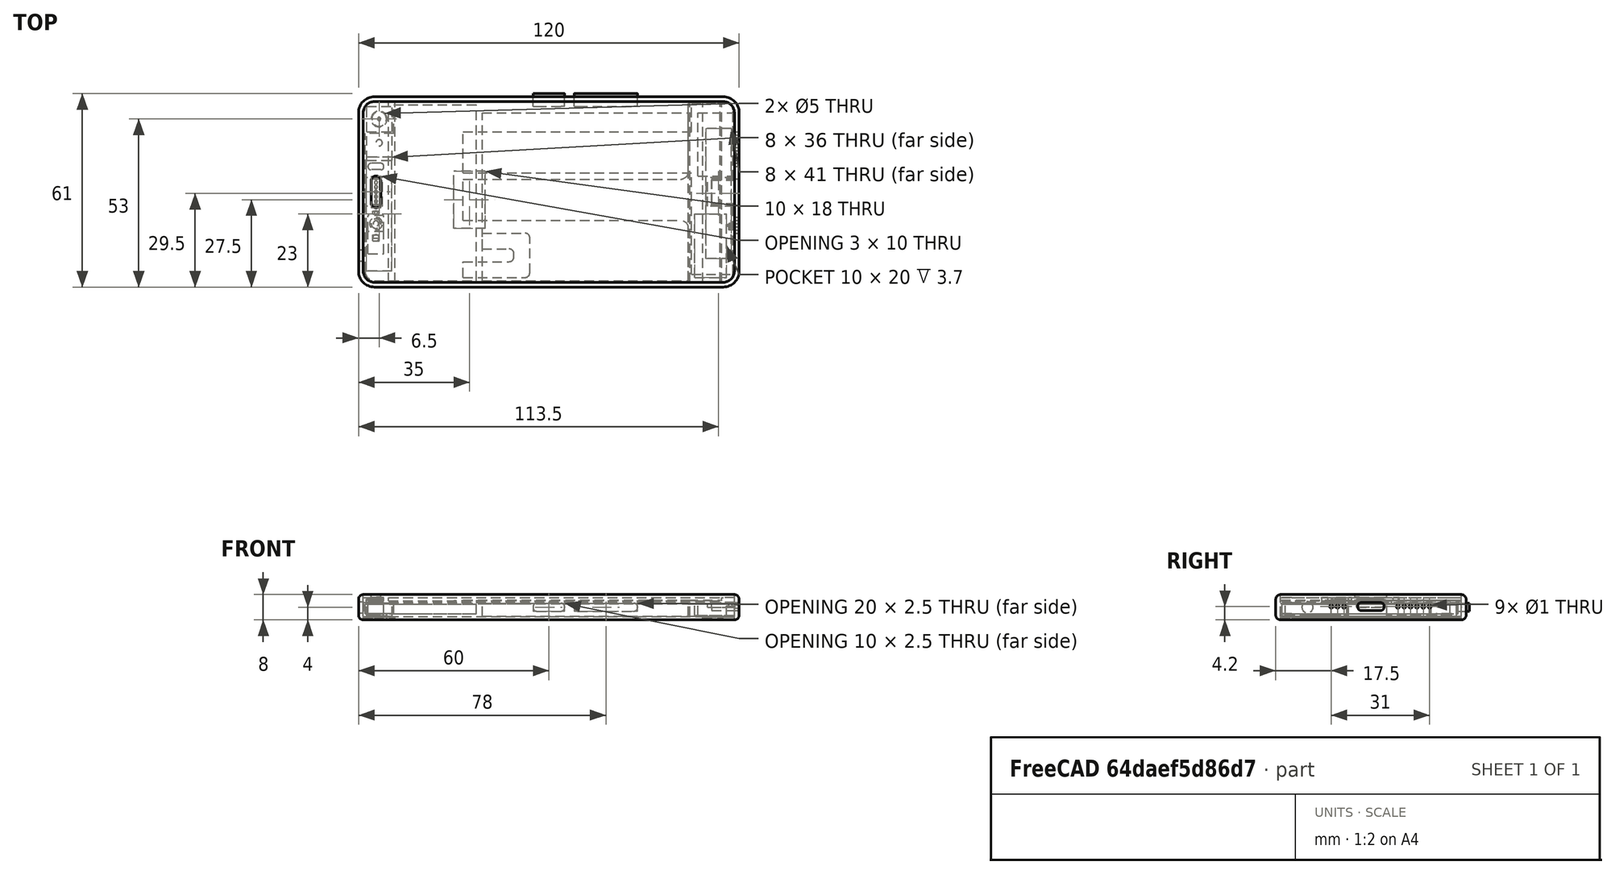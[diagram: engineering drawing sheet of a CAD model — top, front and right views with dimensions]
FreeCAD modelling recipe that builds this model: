
FCSTD DOCUMENT  (FreeCAD 0.16R6706 (Git))
Label: device
License: All rights reserved
LicenseURL: http://en.wikipedia.org/wiki/All_rights_reserved
objects: Part::Box×52, Part::Cut×34, Part::Cylinder×32, Part::Fillet×25, Part::MultiFuse×20, Part::Sphere×4, Part::Chamfer×1
note: 168 computed .brp shape members not serialized (recipe doc carries the construction recipe); baked Part::Feature solids carry a one-line shape summary decoded from their .brp

FEATURE [Part::Box] Box  label="Cubo"
  Height = 8
  Length = 120
  Width = 60
FEATURE [Part::Box] Box001  label="Cubo001"
  Height = 8
  Length = 117
  Placement = pos=(1.5,1.5,0) rot=(0,0,1;0rad)
  Width = 57
FEATURE [Part::Fillet] Fillet
  Base = -> Box
  Edges = 4 edges r=5: [Edge1,Edge3,Edge5,Edge7]
FEATURE [Part::Fillet] Fillet001
  Base = -> Fillet
  Edges = 16 edges r=1.5: [Edge1,Edge4,Edge5,Edge6,Edge7,Edge8,Edge9,Edge10,Edge11,Edge12,Edge14,Edge16,Edge17,Edge18,Edge19,Edge20]
FEATURE [Part::Fillet] Fillet002
  Base = -> Box001
  Edges = 4 edges r=3.5: [Edge1,Edge3,Edge5,Edge7]
  Placement = pos=(0,0,1) rot=(0,0,1;0rad)
FEATURE [Part::Box] Box002  label="Cubo002"
  Height = 1
  Length = 117
  Placement = pos=(1.5,1.5,0) rot=(0,0,1;0rad)
  Width = 57
FEATURE [Part::Fillet] Fillet003
  Base = -> Box002
  Edges = 4 edges r=3.5: [Edge1,Edge3,Edge5,Edge7]
  Placement = pos=(0,0,7) rot=(0,0,1;0rad)
FEATURE [Part::Cut] Cut
  Base = -> Fillet001
  Tool = -> Fillet002
FEATURE [Part::Box] Box003  label="Cubo003"
  Height = 1
  Length = 8
  Placement = pos=(1.5,1.5,0) rot=(0,0,1;0rad)
  Width = 57
FEATURE [Part::Box] Box004  label="Cubo004"
  Height = 1
  Length = 4
  Placement = pos=(114.5,1.5,0) rot=(0,0,1;0rad)
  Width = 57
FEATURE [Part::MultiFuse] Fusion
  Placement = pos=(0,0,6) rot=(0,0,1;0rad)
  Shapes = -> [Box004,Box003]
FEATURE [Part::Fillet] Fillet004
  Base = -> Fusion
  Edges = 4 edges r=3.5: [Edge5,Edge7,Edge13,Edge15]
FEATURE [Part::Box] Box005  label="Screen"
  Height = 1
  Length = 105
  Placement = pos=(9.5,1.5,6) rot=(0,0,1;0rad)
  Width = 57
FEATURE [Part::Box] Box006  label="Cubo006"
  Height = 0.5
  Length = 117
  Placement = pos=(1.5,1.5,0) rot=(0,0,1;0rad)
  Width = 57
FEATURE [Part::Fillet] Fillet005
  Base = -> Box006
  Edges = 4 edges r=3.5: [Edge1,Edge3,Edge5,Edge7]
  Placement = pos=(0,0,5.5) rot=(0,0,1;0rad)
FEATURE [Part::Box] Box007  label="Cubo007"
  Height = 10
  Length = 3
  Placement = pos=(4,25,0) rot=(0,0,1;0rad)
  Width = 10
FEATURE [Part::Fillet] Fillet006
  Base = -> Box007
  Edges = 4 edges r=1.4: [Edge1,Edge3,Edge5,Edge7]
FEATURE [Part::Cut] Cut001  label="TouchScreen"
  Base = -> Fillet003
  Tool = -> Fillet006
FEATURE [Part::Box] Box009  label="Cubo009"
  Height = 10
  Length = 5
  Placement = pos=(3,37,0) rot=(0,0,1;0rad)
  Width = 2
FEATURE [Part::Fillet] Fillet007
  Base = -> Box009
  Edges = 4 edges r=0.9: [Edge1,Edge3,Edge5,Edge7]
FEATURE [Part::Cut] Cut002
  Base = -> Fillet004
  Tool = -> Fillet007
FEATURE [Part::Cylinder] Cylinder  label="Cilindro"
  Angle = 360
  Height = 10
  Placement = pos=(5.5,20,0) rot=(0,0,1;0rad)
  Radius = 2
FEATURE [Part::Cut] Cut003
  Base = -> Cut002
  Tool = -> Cylinder
FEATURE [Part::Cylinder] Cylinder003  label="Cilindro002"
  Angle = 360
  Height = 10
  Placement = pos=(5.5,23.5,0) rot=(0,0,1;0rad)
  Radius = 0.5
FEATURE [Part::Cut] Cut004
  Base = -> Cut003
  Tool = -> Cylinder003
FEATURE [Part::Cylinder] Cylinder004  label="Cilindro003"
  Angle = 360
  Height = 10
  Placement = pos=(5.5,15.5,0) rot=(0,0,1;0rad)
  Radius = 1
FEATURE [Part::Cut] Cut006
  Base = -> Cut004
  Tool = -> Cylinder004
FEATURE [Part::Cylinder] Cylinder005  label="Camera001"
  Angle = 360
  Height = 10
  Placement = pos=(6.5,53,-3) rot=(0,0,1;0rad)
  Radius = 2.5
FEATURE [Part::Cylinder] Cylinder006  label="Flash"
  Angle = 360
  Height = 10
  Placement = pos=(6.5,45.5,-3) rot=(0,0,1;0rad)
  Radius = 1
FEATURE [Part::MultiFuse] Fusion001  label="Camera"
  Shapes = -> [Cylinder005,Cylinder006]
FEATURE [Part::Cylinder] Cylinder007  label="Camera lent"
  Angle = 360
  Height = 1
  Placement = pos=(6.5,53,0) rot=(0,0,1;0rad)
  Radius = 2.5
FEATURE [Part::Cut] Cut007
  Base = -> Cut
  Tool = -> Fusion001
FEATURE [Part::Cylinder] Cylinder008  label="Flash lens"
  Angle = 360
  Height = 1
  Placement = pos=(6.5,45.5,0) rot=(0,0,1;0rad)
  Radius = 1
FEATURE [Part::Box] Box010  label="Cubo010"
  Height = 0.2
  Length = 3
  Placement = pos=(4,25,0) rot=(0,0,1;0rad)
  Width = 10
FEATURE [Part::Fillet] Fillet008  label="Speaker bezel"
  Base = -> Box010
  Edges = 4 edges r=1.4: [Edge1,Edge3,Edge5,Edge7]
  Placement = pos=(0,0,7) rot=(0,0,1;0rad)
FEATURE [Part::Box] Box011  label="Cubo011"
  Height = 10
  Length = 2.5
  Placement = pos=(4.2,26,0) rot=(0,0,1;0rad)
  Width = 8
FEATURE [Part::Cut] Cut008
  Base = -> Cut006
  Tool = -> Box011
FEATURE [Part::Box] Box012  label="Back Camera"
  Height = 4.2
  Length = 8
  Placement = pos=(2.6,49,1.2) rot=(0,0,1;0rad)
  Width = 8
FEATURE [Part::Box] Box013  label="Cubo013"
  Height = 3
  Length = 35
  Placement = pos=(2.1,2,2.5) rot=(0,0,1;0rad)
  Width = 55.5
FEATURE [Part::Fillet] Fillet009
  Base = -> Box013
  Edges = 1 edges r=3: [Edge1]
FEATURE [Part::Box] Box014  label="Back Camera001"
  Height = 4.2
  Length = 9
  Placement = pos=(2.1,48.5,1.6) rot=(0,0,1;0rad)
  Width = 9
FEATURE [Part::Cut] Cut009  label="Cut029"
  Base = -> Fillet009
  Placement = pos=(0,0,-0.5) rot=(0,0,1;0rad)
  Tool = -> Box014
FEATURE [Part::Box] Box015  label="Battery"
  Height = 4
  Length = 65
  Placement = pos=(39,2,1.2) rot=(0,0,1;0rad)
  Width = 53
FEATURE [Part::Box] Box016  label="Cubo015"
  Height = 4
  Length = 14
  Placement = pos=(104.5,1.5,1.2) rot=(0,0,1;0rad)
  Width = 57
FEATURE [Part::Fillet] Fillet010
  Base = -> Box016
  Edges = 2 edges r=3.5: [Edge5,Edge7]
FEATURE [Part::MultiFuse] Fusion002  label="Fusion015"
  Shapes = -> [Fillet005,Cut008]
FEATURE [Part::Cylinder] Cylinder009  label="Camera lent001"
  Angle = 360
  Height = 1
  Placement = pos=(6.5,53,1) rot=(0,0,1;0rad)
  Radius = 2.5
FEATURE [Part::Cut] Cut010  label="MainCamera"
  Base = -> Box012
  Tool = -> Cylinder009
FEATURE [Part::Cylinder] Cylinder010  label="Camera lent002"
  Angle = 360
  Height = 1
  Placement = pos=(6.5,53,1) rot=(0,0,1;0rad)
  Radius = 2.3
FEATURE [Part::Sphere] Sphere001  label="Esfera"
  Angle1 = -90
  Angle2 = 90
  Angle3 = 360
  Placement = pos=(6.5,53,1) rot=(0,0,1;0rad)
  Radius = 0.5
FEATURE [Part::Cut] Cut011
  Base = -> Cylinder007
  Tool = -> Sphere001
FEATURE [Part::Sphere] Sphere002  label="Esfera001"
  Angle1 = -90
  Angle2 = 90
  Angle3 = 360
  Placement = pos=(6.5,53,1) rot=(0,0,1;0rad)
  Radius = 0.5
FEATURE [Part::Box] Box035  label="Cubo029"
  Height = 2.45
  Length = 8.65
  Width = 8.3
FEATURE [Part::Fillet] Fillet022  label="USB-C"
  Base = -> Box035
  Edges = 4 edges r=1: [Edge9,Edge10,Edge11,Edge12]
  Placement = pos=(111.35,25.85,3) rot=(0,0,1;0rad)
FEATURE [Part::Cylinder] Cylinder011  label="Cilindro004"
  Angle = 360
  Height = 10
  Placement = pos=(113,48.5,4.2) rot=(0.57735,0.57735,0.57735;2.0944rad)
  Radius = 0.5
FEATURE [Part::Cylinder] Cylinder012  label="Cilindro005"
  Angle = 360
  Height = 10
  Placement = pos=(113,11.5,4.2) rot=(0.57735,0.57735,0.57735;2.0944rad)
  Radius = 0.5
FEATURE [Part::Cylinder] Cylinder013  label="Cilindro006"
  Angle = 360
  Height = 10
  Placement = pos=(113,46.5,4.2) rot=(0.57735,0.57735,0.57735;2.0944rad)
  Radius = 0.5
FEATURE [Part::Cylinder] Cylinder014  label="Cilindro007"
  Angle = 360
  Height = 10
  Placement = pos=(113,13.5,4.2) rot=(0.57735,0.57735,0.57735;2.0944rad)
  Radius = 0.5
FEATURE [Part::Cylinder] Cylinder015  label="Cilindro008"
  Angle = 360
  Height = 10
  Placement = pos=(113,44.5,4.2) rot=(0.57735,0.57735,0.57735;2.0944rad)
  Radius = 0.5
FEATURE [Part::Cylinder] Cylinder016  label="Cilindro009"
  Angle = 360
  Height = 10
  Placement = pos=(113,15.5,4.2) rot=(0.57735,0.57735,0.57735;2.0944rad)
  Radius = 0.5
FEATURE [Part::MultiFuse] Fusion003  label="mic holes"
  Placement = pos=(0,6,0) rot=(0,0,1;0rad)
  Shapes = -> [Cylinder012,Cylinder014,Cylinder016]
FEATURE [Part::MultiFuse] Fusion004
  Placement = pos=(0,-6,0) rot=(0,0,1;0rad)
  Shapes = -> [Cylinder013,Cylinder011,Cylinder015]
FEATURE [Part::Cylinder] Cylinder017  label="Cilindro010"
  Angle = 360
  Height = 10
  Placement = pos=(113,48.5,4.2) rot=(0.57735,0.57735,0.57735;2.0944rad)
  Radius = 0.5
FEATURE [Part::Cylinder] Cylinder018  label="Cilindro011"
  Angle = 360
  Height = 10
  Placement = pos=(113,46.5,4.2) rot=(0.57735,0.57735,0.57735;2.0944rad)
  Radius = 0.5
FEATURE [Part::Cylinder] Cylinder019  label="Cilindro012"
  Angle = 360
  Height = 10
  Placement = pos=(113,44.5,4.2) rot=(0.57735,0.57735,0.57735;2.0944rad)
  Radius = 0.5
FEATURE [Part::MultiFuse] Fusion005
  Shapes = -> [Cylinder018,Cylinder017,Cylinder019]
FEATURE [Part::MultiFuse] Fusion006  label="speaker holes"
  Shapes = -> [Fusion005,Fusion004]
FEATURE [Part::MultiFuse] Fusion007  label="Bot holes"
  Shapes = -> [Fusion003,Fillet022,Fusion006]
FEATURE [Part::Cut] Cut012
  Base = -> Cut007
  Tool = -> Fusion007
FEATURE [Part::Cut] Cut013
  Base = -> Fillet010
  Tool = -> Fillet022
FEATURE [Part::Cylinder] Cylinder020  label="Cilindro013"
  Angle = 360
  Height = 10
  Placement = pos=(113,19.5,4.2) rot=(0.57735,0.57735,0.57735;2.0944rad)
  Radius = 0.25
FEATURE [Part::Cut] Cut014
  Base = -> Cut013
  Tool = -> Cylinder020
FEATURE [Part::Box] Box036  label="Tapic engine"
  Height = 3.7
  Length = 10
  Placement = pos=(106,3,1.5) rot=(0,0,1;0rad)
  Width = 20
FEATURE [Part::Box] Box037  label="Speaker hole"
  Height = 3.7
  Length = 14
  Placement = pos=(107,35,1.5) rot=(0,0,1;0rad)
  Width = 20
FEATURE [Part::Cut] Cut015  label="Cut022"
  Base = -> Cut014
  Tool = -> Box037
FEATURE [Part::Box] Box038  label="Speaker"
  Height = 3.7
  Length = 11.5
  Placement = pos=(107,35,1.5) rot=(0,0,1;0rad)
  Width = 20
FEATURE [Part::Box] Box039  label="Cubo030"
  Height = 0.8
  Length = 10
  Placement = pos=(1.5,1.5,0) rot=(0,0,1;0rad)
  Width = 57
FEATURE [Part::Fillet] Fillet023
  Base = -> Box039
  Edges = 2 edges r=3.5: [Edge1,Edge3]
FEATURE [Part::Box] Box041  label="Cubo031"
  Height = 0.8
  Length = 10
  Placement = pos=(108.5,1.5,0) rot=(0,0,1;0rad)
  Width = 57
FEATURE [Part::Fillet] Fillet024
  Base = -> Box041
  Edges = 2 edges r=3.5: [Edge5,Edge7]
FEATURE [Part::MultiFuse] Fusion008
  Shapes = -> [Fillet023,Fillet024]
FEATURE [Part::Box] Box042  label="Cubo032"
  Height = 0.8
  Length = 10
  Placement = pos=(1.5,1.5,0) rot=(0,0,1;0rad)
  Width = 57
FEATURE [Part::Fillet] Fillet025
  Base = -> Box042
  Edges = 2 edges r=3.5: [Edge1,Edge3]
FEATURE [Part::Box] Box043  label="Cubo033"
  Height = 0.8
  Length = 10
  Placement = pos=(108.5,1.5,0) rot=(0,0,1;0rad)
  Width = 57
FEATURE [Part::Fillet] Fillet026
  Base = -> Box043
  Edges = 2 edges r=3.5: [Edge5,Edge7]
FEATURE [Part::MultiFuse] Fusion009
  Shapes = -> [Fillet025,Fillet026]
FEATURE [Part::Cut] Cut016
  Base = -> Cut012
  Tool = -> Fusion008
FEATURE [Part::Cut] Cut017
  Base = -> Fusion009
  Tool = -> Cut011
FEATURE [Part::Cut] Cut018  label="Antenna"
  Base = -> Cut017
  Tool = -> Cylinder008
FEATURE [Part::Box] Box044  label="Cubo034"
  Height = 10
  Length = 8
  Placement = pos=(2.5,5,0) rot=(0,0,1;0rad)
  Width = 36
FEATURE [Part::Box] Box045  label="Cubo035"
  Height = 10
  Length = 8
  Placement = pos=(109.5,9,0) rot=(0,0,1;0rad)
  Width = 41
FEATURE [Part::MultiFuse] Fusion010
  Shapes = -> [Box045,Box044]
FEATURE [Part::Cut] Cut019  label="Cut018"
  Base = -> Cut016
  Tool = -> Fusion010
FEATURE [Part::Box] Box046  label="Cubo036"
  Height = 2.5
  Length = 10
  Placement = pos=(55,57,2.75) rot=(0,0,1;0rad)
  Width = 4
FEATURE [Part::Box] Box047  label="Cubo037"
  Height = 2.5
  Length = 20
  Placement = pos=(68,57,2.75) rot=(0,0,1;0rad)
  Width = 4
FEATURE [Part::Fillet] Fillet027  label="PowerButtonr"
  Base = -> Box046
  Edges = 4 edges r=1.2: [Edge2,Edge4,Edge6,Edge8]
FEATURE [Part::Fillet] Fillet028  label="VolumeButtonr"
  Base = -> Box047
  Edges = 4 edges r=1.2: [Edge2,Edge4,Edge6,Edge8]
FEATURE [Part::MultiFuse] Fusion011  label="Buttonsr"
  Shapes = -> [Fillet027,Fillet028]
FEATURE [Part::Cut] Cut020  label="CUT"
  Base = -> Cut019
  Tool = -> Fusion011
FEATURE [Part::Box] Box048  label="Cubo038"
  Height = 2.5
  Length = 10
  Placement = pos=(55,57,2.75) rot=(0,0,1;0rad)
  Width = 4
FEATURE [Part::Box] Box049  label="Cubo039"
  Height = 2.5
  Length = 20
  Placement = pos=(68,57,2.75) rot=(0,0,1;0rad)
  Width = 4
FEATURE [Part::Fillet] Fillet029  label="PowerButton"
  Base = -> Box048
  Edges = 4 edges r=1.2: [Edge2,Edge4,Edge6,Edge8]
FEATURE [Part::Fillet] Fillet030  label="VolumeButton"
  Base = -> Box049
  Edges = 4 edges r=1.2: [Edge2,Edge4,Edge6,Edge8]
FEATURE [Part::MultiFuse] Fusion012  label="Buttons"
  Shapes = -> [Fillet029,Fillet030]
FEATURE [Part::Cylinder] Cylinder021  label="Camera lent003"
  Angle = 360
  Height = 1
  Placement = pos=(6.5,53,0) rot=(0,0,1;0rad)
  Radius = 2.5
FEATURE [Part::Sphere] Sphere003  label="Esfera002"
  Angle1 = -90
  Angle2 = 90
  Angle3 = 360
  Placement = pos=(6.5,53,1) rot=(0,0,1;0rad)
  Radius = 0.5
FEATURE [Part::Cut] Cut021
  Base = -> Cylinder021
  Tool = -> Sphere003
FEATURE [Part::Box] Box050  label="Cubo040"
  Height = 0.2
  Length = 15
  Placement = pos=(39,12,5.1) rot=(0,0,1;0rad)
  Width = 5
FEATURE [Part::Box] Box051  label="Cubo041"
  Height = 0.2
  Length = 21
  Placement = pos=(33,3,5.1) rot=(0,0,1;0rad)
  Width = 5
FEATURE [Part::Box] Box052  label="Cubo042"
  Height = 0.2
  Length = 5
  Placement = pos=(49,3,5.1) rot=(0,0,1;0rad)
  Width = 11
FEATURE [Part::MultiFuse] Fusion013
  Shapes = -> [Box050,Box051,Box052]
FEATURE [Part::Fillet] Fillet031  label="Battery Flex"
  Base = -> Fusion013
  Edges = 4 edges r=1.5: [Edge6,Edge9,Edge13,Edge24]
FEATURE [Part::Box] Box053  label="Cubo043"
  Height = 10
  Length = 10
  Placement = pos=(110,25.5,4) rot=(0,0,1;0rad)
  Width = 9
FEATURE [Part::Cut] Cut022  label="Cut023"
  Base = -> Cut015
  Tool = -> Box053
FEATURE [Part::Box] Box054  label="Tapic engine001"
  Height = 3.7
  Length = 10
  Placement = pos=(106,3,1.5) rot=(0,0,1;0rad)
  Width = 20
FEATURE [Part::Cut] Cut023  label="Cut024"
  Base = -> Cut022
  Tool = -> Box054
FEATURE [Part::Box] Box055  label="Cubo044"
  Height = 1.5
  Length = 1
  Placement = pos=(116.8,18,4) rot=(0,0,1;0rad)
  Width = 2
FEATURE [Part::Chamfer] Chamfer
  Base = -> Box055
  Edges = 4 edges r=0.4: [Edge4,Edge8,Edge9,Edge11]
FEATURE [Part::Cut] Cut024  label="Cut025"
  Base = -> Cut023
  Tool = -> Chamfer
FEATURE [Part::Box] Box056  label="Cubo045"
  Height = 0.2
  Length = 81
  Placement = pos=(33,36,5.1) rot=(0,0,1;0rad)
  Width = 13
FEATURE [Part::Box] Box057  label="Cubo046"
  Height = 0.2
  Length = 13
  Placement = pos=(105,4,5.1) rot=(0,0,1;0rad)
  Width = 54
FEATURE [Part::Fillet] Fillet032
  Base = -> Box057
  Edges = 1 edges r=2: [Edge7]
FEATURE [Part::MultiFuse] Fusion014
  Shapes = -> [Box056,Fillet032]
FEATURE [Part::Box] Box058  label="Cubo047"
  Height = 2.45
  Length = 8.65
  Width = 8.3
FEATURE [Part::Fillet] Fillet033  label="USB-C001"
  Base = -> Box058
  Edges = 4 edges r=1: [Edge9,Edge10,Edge11,Edge12]
  Placement = pos=(111.35,25.85,3) rot=(0,0,1;0rad)
FEATURE [Part::Box] Box059  label="Cubo048"
  Height = 2.45
  Length = 8.65
  Width = 8.3
FEATURE [Part::Fillet] Fillet034  label="USB-C002"
  Base = -> Box059
  Edges = 4 edges r=1: [Edge9,Edge10,Edge11,Edge12]
  Placement = pos=(111.35,25.85,3) rot=(0,0,1;0rad)
FEATURE [Part::Cut] Cut025  label="MainFlex"
  Base = -> Fusion014
  Tool = -> Fillet033
FEATURE [Part::Box] Box060  label="Cubo049"
  Height = 0.2
  Length = 81
  Placement = pos=(33,21,6.1) rot=(0,0,1;0rad)
  Width = 13
FEATURE [Part::Box] Box061  label="Cubo050"
  Height = 2.2
  Length = 10
  Placement = pos=(30,18.5,5.1) rot=(0,0,1;0rad)
  Width = 18
FEATURE [Part::Cut] Cut026  label="Cut032"
  Base = -> Fusion002
  Tool = -> Box061
FEATURE [Part::Box] Box062  label="Cubo051"
  Height = 0.2
  Length = 10
  Placement = pos=(104,1.7,6.1) rot=(0,0,1;0rad)
  Width = 56.5
FEATURE [Part::MultiFuse] Fusion015  label="Fusion016"
  Shapes = -> [Box062,Box060]
FEATURE [Part::Fillet] Fillet035  label="Screen Flex"
  Base = -> Fusion015
  Edges = 2 edges r=2.5: [Edge6,Edge15]
FEATURE [Part::Cut] Cut027
  Base = -> Cut026
  Tool = -> Cylinder
FEATURE [Part::Box] Box063  label="Cubo052"
  Height = 10
  Length = 5
  Placement = pos=(3,17.5,-3) rot=(0,0,1;0rad)
  Width = 5
FEATURE [Part::Box] Box064  label="Cubo053"
  Height = 4.5
  Length = 5
  Placement = pos=(3,17.5,1.5) rot=(0,0,1;0rad)
  Width = 5
FEATURE [Part::Cut] Cut028
  Base = -> Cut009
  Tool = -> Box063
FEATURE [Part::Cylinder] Cylinder022  label="Cilindro014"
  Angle = 360
  Height = 3
  Placement = pos=(5.5,20,3.5) rot=(0,0,1;0rad)
  Radius = 1.5
FEATURE [Part::Sphere] Sphere  label="Esfera003"
  Angle1 = -90
  Angle2 = 90
  Angle3 = 360
  Placement = pos=(5.5,20,6) rot=(0,0,1;0rad)
  Radius = 1
FEATURE [Part::MultiFuse] Fusion016  label="Front-Facing Camera"
  Shapes = -> [Box064,Cylinder022,Sphere]
FEATURE [Part::Box] Box065  label="Front-Facing Camera Flex"
  Height = 0.2
  Length = 5
  Placement = pos=(3,10.5,1.5) rot=(0,0,1;0rad)
  Width = 7
FEATURE [Part::Box] Box066  label="MainCameraFlex"
  Height = 0.2
  Length = 8
  Placement = pos=(2.6,40,5.2) rot=(0,0,1;0rad)
  Width = 9
FEATURE [Part::MultiFuse] Fusion017
  Shapes = -> [Cylinder004,Cylinder003]
FEATURE [Part::Cut] Cut029  label="Cut030"
  Base = -> Cut027
  Tool = -> Fusion017
FEATURE [Part::Box] Box067  label="NotificationLED"
  Height = 1
  Length = 2
  Placement = pos=(4.5,23,5) rot=(0,0,1;0rad)
  Width = 1
FEATURE [Part::Box] Box068  label="YellowFrontFlash"
  Height = 1
  Length = 2
  Placement = pos=(4.5,14.5,5) rot=(0,0,1;0rad)
  Width = 1
FEATURE [Part::Box] Box069  label="OrangeFrontFlash"
  Height = 1
  Length = 2
  Placement = pos=(4.5,15.5,5) rot=(0,0,1;0rad)
  Width = 1
FEATURE [Part::Box] Box070  label="Cubo054"
  Height = 1.5
  Length = 5
  Placement = pos=(2.5,25.5,5) rot=(0,0,1;0rad)
  Width = 9
FEATURE [Part::Cut] Cut030  label="Cut031"
  Base = -> Cut029
  Tool = -> Box011
FEATURE [Part::Cylinder] Cylinder023  label="Cilindro015"
  Angle = 360
  Height = 10
  Placement = pos=(5.5,27,0) rot=(0,0,1;0rad)
  Radius = 0.5
FEATURE [Part::Cylinder] Cylinder024  label="Cilindro016"
  Angle = 360
  Height = 10
  Placement = pos=(5.5,28.5,0) rot=(0,0,1;0rad)
  Radius = 0.5
FEATURE [Part::Cylinder] Cylinder025  label="Cilindro017"
  Angle = 360
  Height = 10
  Placement = pos=(5.5,30,0) rot=(0,0,1;0rad)
  Radius = 0.5
FEATURE [Part::Cylinder] Cylinder026  label="Cilindro018"
  Angle = 360
  Height = 10
  Placement = pos=(5.5,31.5,0) rot=(0,0,1;0rad)
  Radius = 0.5
FEATURE [Part::Cylinder] Cylinder027  label="Cilindro019"
  Angle = 360
  Height = 10
  Placement = pos=(5.5,33,0) rot=(0,0,1;0rad)
  Radius = 0.5
FEATURE [Part::MultiFuse] Fusion018
  Placement = pos=(0,0,6) rot=(0,0,1;0rad)
  Shapes = -> [Cylinder027,Cylinder023,Cylinder024,Cylinder025,Cylinder026]
FEATURE [Part::Cut] Cut031  label="Cut033"
  Base = -> Box070
  Tool = -> Fusion018
FEATURE [Part::Box] Box071  label="TopSpeaker001"
  Height = 1.5
  Length = 5
  Placement = pos=(2.5,25.5,5) rot=(0,0,1;0rad)
  Width = 9
FEATURE [Part::Cylinder] Cylinder028  label="Cilindro020"
  Angle = 360
  Height = 10
  Placement = pos=(5.5,27,0) rot=(0,0,1;0rad)
  Radius = 0.5
FEATURE [Part::Cylinder] Cylinder029  label="Cilindro021"
  Angle = 360
  Height = 10
  Placement = pos=(5.5,28.5,0) rot=(0,0,1;0rad)
  Radius = 0.5
FEATURE [Part::Cylinder] Cylinder030  label="Cilindro022"
  Angle = 360
  Height = 10
  Placement = pos=(5.5,30,0) rot=(0,0,1;0rad)
  Radius = 0.5
FEATURE [Part::Cylinder] Cylinder031  label="Cilindro023"
  Angle = 360
  Height = 10
  Placement = pos=(5.5,31.5,0) rot=(0,0,1;0rad)
  Radius = 0.5
FEATURE [Part::Cylinder] Cylinder032  label="Cilindro024"
  Angle = 360
  Height = 10
  Placement = pos=(5.5,33,0) rot=(0,0,1;0rad)
  Radius = 0.5
FEATURE [Part::MultiFuse] Fusion019
  Placement = pos=(0,0,6) rot=(0,0,1;0rad)
  Shapes = -> [Cylinder032,Cylinder028,Cylinder029,Cylinder030,Cylinder031]
FEATURE [Part::Cut] Cut032  label="TopSpeaker"
  Base = -> Box071
  Tool = -> Fusion019
FEATURE [Part::Cut] Cut033  label="Frame"
  Base = -> Cut030
  Tool = -> Cut031
FEATURE [Part::Cylinder] Cylinder034  label="Cilindro026"
  Angle = 360
  Height = 10
  Placement = pos=(-1,10,4) rot=(0.57735,0.57735,0.57735;2.0944rad)
  Radius = 1.75
FEATURE [Part::Cut] Cut034  label="Chassis"
  Base = -> Cut020
  Tool = -> Cylinder034
